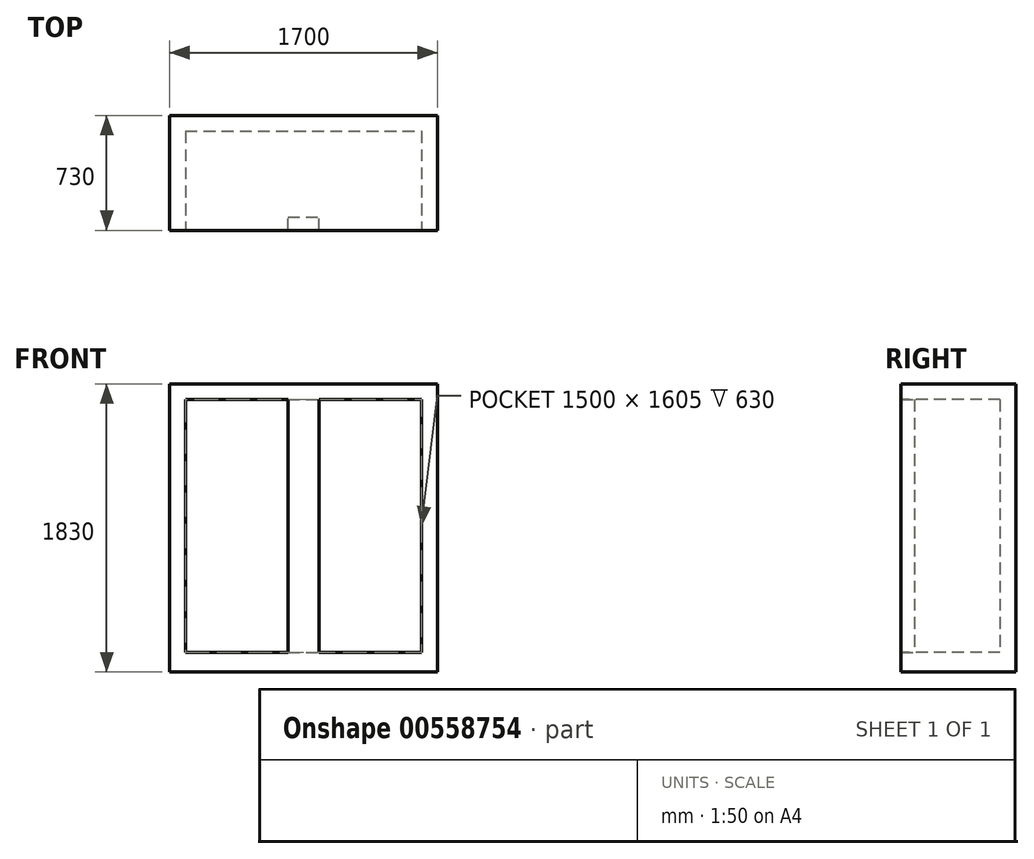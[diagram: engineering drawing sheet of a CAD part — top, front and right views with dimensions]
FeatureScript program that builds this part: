
annotation { "Feature Type Name" : "Feature", "Feature Type Description" : "" }
export const myFeature = defineFeature(function(context is Context, id is Id, definition is map)
    precondition{}
    {
        {
            var Q0;
            Q0=qCreatedBy(makeId("Front.planeOp"),FACE);
            var sketch = newSketch(context, id + "F0", { "sketchPlane" : qUnion([Q0])});
            skLineSegment(sketch, "E0.bottom", {"start": v(-850, 915) * mm, "end": v(850, 915) * mm});
            skLineSegment(sketch, "E0.top", {"start": v(-850, -915) * mm, "end": v(850, -915) * mm});
            skLineSegment(sketch, "E0.left", {"start": v(-850, 915) * mm, "end": v(-850, -915) * mm});
            skLineSegment(sketch, "E0.right", {"start": v(850, 915) * mm, "end": v(850, -915) * mm});
            skPoint(sketch, "E0.middle", {"position": v(0, 0) * mm});
            skSolve(sketch);
        }
        {
            var Q0;
            Q0=makeQuery(id+"F0.imprint","IMPRINT",FACE,{"disambiguationData":[TD([[makeQuery(id+"F0.imprint","IMPRINT",EDGE,{"derivedFrom":sQuery(id+"F0.wireOp",EDGE,"E0.bottom")}),-1.0]])]});
            extrude(context, id + "F1", {"entities" : qUnion([Q0]), "depth" : 730 * mm, "offsetDistance" : 25 * mm, "symmetric" : true});
        }
        {
            var Q0;
            Q0=makeQuery(id+"F1.opExtrude","CAP_FACE",FACE,{"disambiguationData":[OSD([sQuery(id+"F0.wireOp",EDGE,"E0.bottom"),sQuery(id+"F0.wireOp",EDGE,"E0.top"),sQuery(id+"F0.wireOp",EDGE,"E0.left"),sQuery(id+"F0.wireOp",EDGE,"E0.right")])],"isStart":false});
            var sketch = newSketch(context, id + "F2", { "sketchPlane" : qUnion([Q0])});
            skLineSegment(sketch, "E1.bottom", {"start": v(-750, 815) * mm, "end": v(750, 815) * mm});
            skLineSegment(sketch, "E1.top", {"start": v(-750, -815) * mm, "end": v(750, -815) * mm});
            skLineSegment(sketch, "E1.left", {"start": v(-750, 815) * mm, "end": v(-750, -815) * mm});
            skLineSegment(sketch, "E1.right", {"start": v(750, 815) * mm, "end": v(750, -815) * mm});
            skPoint(sketch, "E1.middle", {"position": v(0, 0) * mm});
            skSolve(sketch);
        }
        {
            var Q0;
            Q0 = qSketchRegion(id + "F2", true);
            extrude(context, id + "F3", {"entities" : qUnion([Q0]), "operationType" : NewBodyOperationType.REMOVE, "oppositeDirection" : true, "depth" : 630 * mm, "offsetDistance" : 25 * mm});
        }
        {
            var Q0;
            Q0=makeQuery(id+"F3.boolean.opBoolean","COPY",FACE,{"derivedFrom":makeQuery(id+"F3.opExtrude","SWEPT_FACE",FACE,{"disambiguationData":[OSD([sQuery(id+"F2.wireOp",EDGE,"E1.top")])]})});
            extrude(context, id + "F4", {"entities" : qUnion([Q0]), "operationType" : NewBodyOperationType.ADD, "depth" : 25 * mm, "offsetDistance" : 25 * mm});
        }
        {
            var Q0;
            Q0=makeQuery(id+"F4.opExtrude","CAP_FACE",FACE,{"disambiguationData":[OSD([sQuery(id+"F2.wireOp",EDGE,"E1.top")])],"isStart":false});
            var sketch = newSketch(context, id + "F5", { "sketchPlane" : qUnion([Q0])});
            skLineSegment(sketch, "E2.bottom", {"start": v(-100, -365) * mm, "end": v(100, -365) * mm});
            skLineSegment(sketch, "E2.top", {"start": v(-100, -280) * mm, "end": v(100, -280) * mm});
            skLineSegment(sketch, "E2.left", {"start": v(-100, -365) * mm, "end": v(-100, -280) * mm});
            skLineSegment(sketch, "E2.right", {"start": v(100, -365) * mm, "end": v(100, -280) * mm});
            skLineSegment(sketch, "E3", {"start": v(0, 265) * mm, "end": v(0, -280) * mm, "construction": true});
            skSolve(sketch);
        }
        {
            var Q0;
            Q0 = qSketchRegion(id + "F5", true);
            extrude(context, id + "F6", {"entities" : qUnion([Q0]), "operationType" : NewBodyOperationType.ADD, "depth" : 1630 * mm, "offsetDistance" : 25 * mm});
        }
    });
